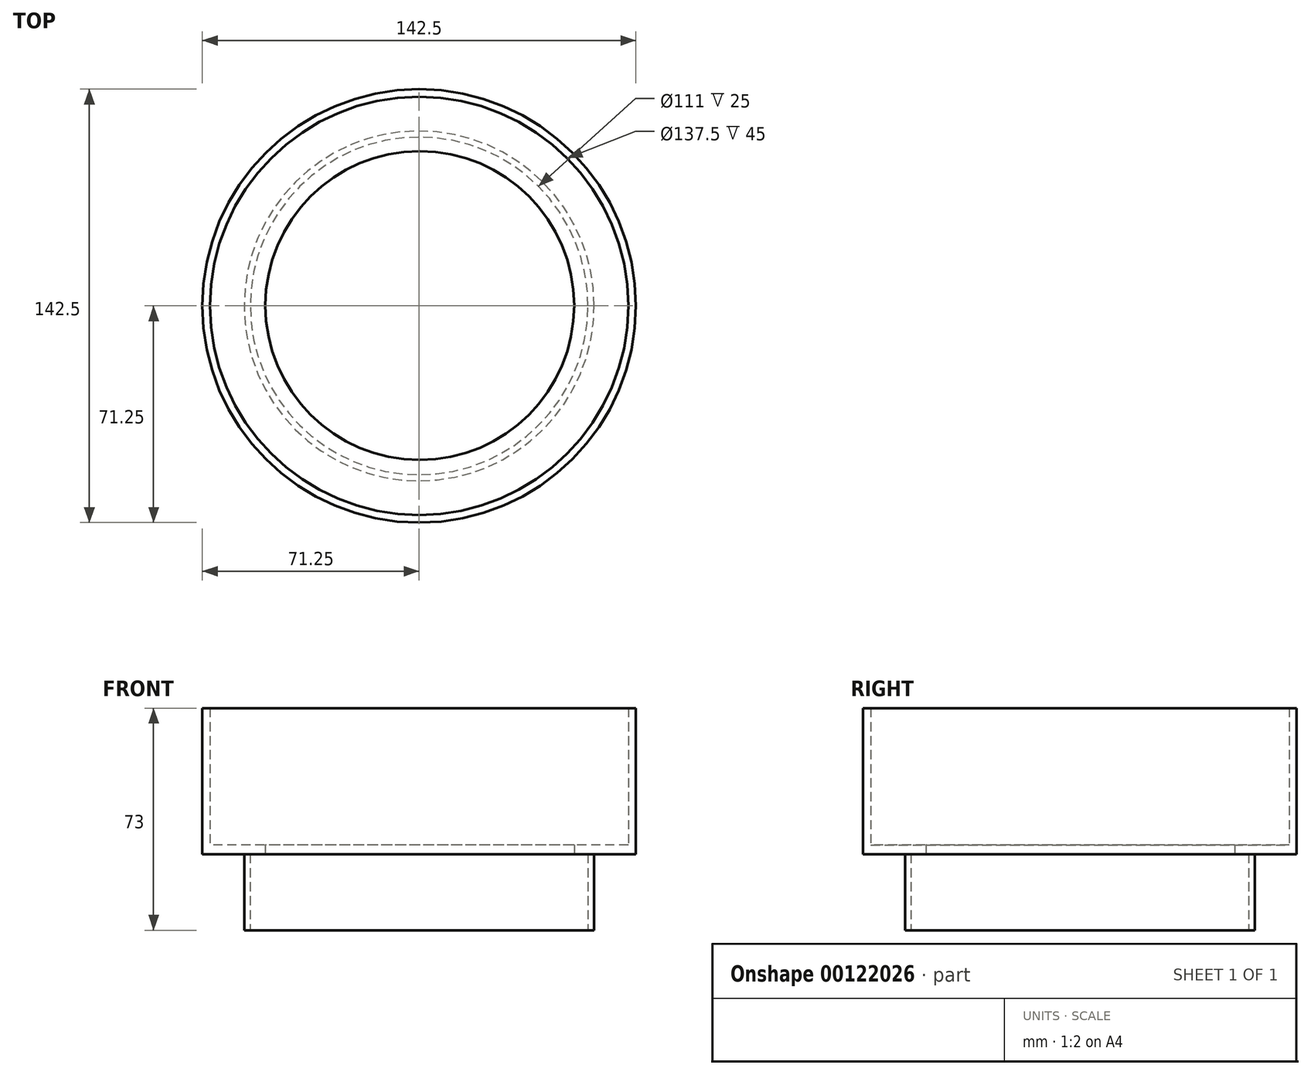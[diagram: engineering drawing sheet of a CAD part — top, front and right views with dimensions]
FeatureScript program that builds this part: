
annotation { "Feature Type Name" : "Feature", "Feature Type Description" : "" }
export const myFeature = defineFeature(function(context is Context, id is Id, definition is map)
    precondition{}
    {
        {
            var Q0;
            Q0=qCreatedBy(makeId("Top.planeOp"),FACE);
            var sketch = newSketch(context, id + "F0", { "sketchPlane" : qUnion([Q0])});
            skCircle(sketch, "E0", {"center": v(0, 0) * mm, "radius": 55.5 * mm});
            skCircle(sketch, "E1.0", {"center": v(0, 0) * mm, "radius": 57.5 * mm});
            skSolve(sketch);
        }
        {
            var Q0;
            Q0=makeQuery(id+"F0.imprint","IMPRINT",FACE,{"disambiguationData":[TD([[makeQuery(id+"F0.imprint","IMPRINT",EDGE,{"derivedFrom":sQuery(id+"F0.wireOp",EDGE,"E0")}),-1.0]])]});
            extrude(context, id + "F1", {"entities" : qUnion([Q0]), "depth" : 25 * mm});
        }
        {
            var Q0;
            Q0=makeQuery(id+"F1.opExtrude","CAP_FACE",FACE,{"disambiguationData":[OSD([sQuery(id+"F0.wireOp",EDGE,"E0"),sQuery(id+"F0.wireOp",EDGE,"E1.0")])],"isStart":false});
            var sketch = newSketch(context, id + "F2", { "sketchPlane" : qUnion([Q0])});
            skCircle(sketch, "E2.0", {"center": v(0, 0) * mm, "radius": 57.5 * mm});
            skCircle(sketch, "E3", {"center": v(0.2, 0.14) * mm, "radius": 50.75 * mm});
            skCircle(sketch, "E4", {"center": v(0, 0) * mm, "radius": 71.25 * mm});
            skSolve(sketch);
        }
        {
            var Q0;
            Q0=makeQuery(id+"F2.imprint","IMPRINT",FACE,{"disambiguationData":[TD([[makeQuery(id+"F2.imprint","IMPRINT",EDGE,{"derivedFrom":sQuery(id+"F2.wireOp",EDGE,"E3")}),-1.0]])]});
            var Q1;
            Q1=makeQuery(id+"F2.imprint","IMPRINT",FACE,{"disambiguationData":[TD([[makeQuery(id+"F2.imprint","IMPRINT",EDGE,{"derivedFrom":sQuery(id+"F2.wireOp",EDGE,"E2.0")}),1.0]])]});
            extrude(context, id + "F3", {"entities" : qUnion([Q0, Q1]), "operationType" : NewBodyOperationType.ADD, "depth" : 3 * mm});
        }
        {
            var Q0;
            Q0=makeQuery(id+"F2.imprint","IMPRINT",FACE,{"disambiguationData":[TD([[makeQuery(id+"F2.imprint","IMPRINT",EDGE,{"derivedFrom":sQuery(id+"F2.wireOp",EDGE,"E2.0")}),-1.0]])]});
            extrude(context, id + "F4", {"entities" : qUnion([Q0]), "operationType" : NewBodyOperationType.ADD, "depth" : 3 * mm});
        }
        {
            var Q0;
            {var subQ0=sQuery(id+"F2.wireOp",EDGE,"E2.0");Q0=makeQuery(id+"F4.boolean.opBoolean","MERGE",FACE,{"derivedFrom":[makeQuery(id+"F3.opExtrude","CAP_FACE",FACE,{"disambiguationData":[OSD([subQ0,sQuery(id+"F2.wireOp",EDGE,"E3")])],"isStart":false}),makeQuery(id+"F4.opExtrude","CAP_FACE",FACE,{"disambiguationData":[OSD([subQ0,sQuery(id+"F2.wireOp",EDGE,"E4")])],"isStart":false})]});}
            var sketch = newSketch(context, id + "F5", { "sketchPlane" : qUnion([Q0])});
            skCircle(sketch, "E5.0", {"center": v(0, 0) * mm, "radius": 71.25 * mm});
            skCircle(sketch, "E6.0", {"center": v(0, 0) * mm, "radius": 68.75 * mm});
            skSolve(sketch);
        }
        {
            var Q0;
            Q0=makeQuery(id+"F5.imprint","IMPRINT",FACE,{"disambiguationData":[TD([[makeQuery(id+"F5.imprint","IMPRINT",EDGE,{"derivedFrom":sQuery(id+"F5.wireOp",EDGE,"E5.0")}),1.0]])]});
            extrude(context, id + "F6", {"entities" : qUnion([Q0]), "operationType" : NewBodyOperationType.ADD, "depth" : 45 * mm});
        }
    });
